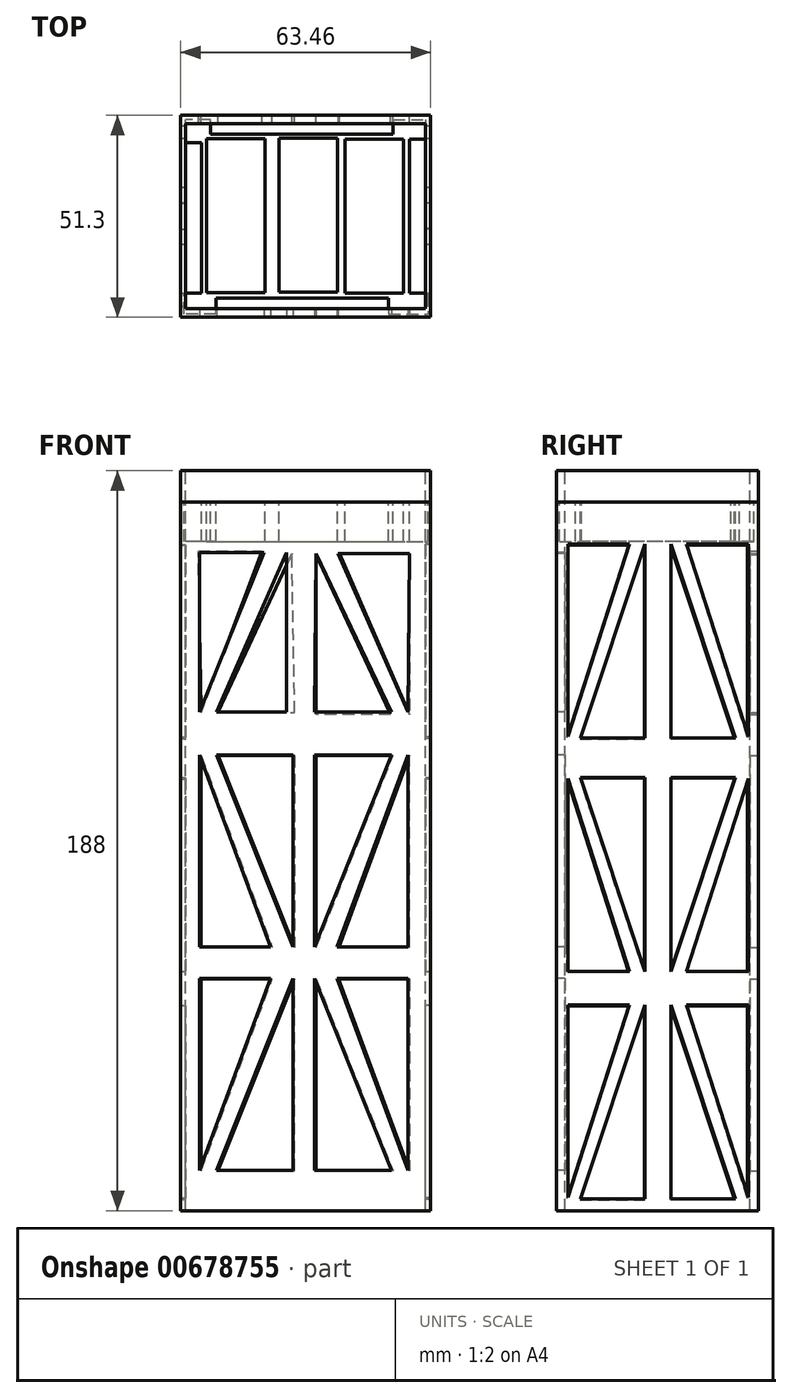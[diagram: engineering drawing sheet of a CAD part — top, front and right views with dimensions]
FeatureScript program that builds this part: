
annotation { "Feature Type Name" : "Feature", "Feature Type Description" : "" }
export const myFeature = defineFeature(function(context is Context, id is Id, definition is map)
    precondition{}
    {
        {
            var Q0;
            Q0=qCreatedBy(makeId("Top.planeOp"),FACE);
            var sketch = newSketch(context, id + "F0", { "sketchPlane" : qUnion([Q0])});
            skLineSegment(sketch, "E0.bottom", {"start": v(-30.5, 23.5) * mm, "end": v(30.5, 23.5) * mm});
            skLineSegment(sketch, "E0.top", {"start": v(-30.5, -23.5) * mm, "end": v(30.5, -23.5) * mm});
            skLineSegment(sketch, "E0.left", {"start": v(-30.5, 23.5) * mm, "end": v(-30.5, -23.5) * mm});
            skLineSegment(sketch, "E0.right", {"start": v(30.5, 23.5) * mm, "end": v(30.5, -23.5) * mm});
            skPoint(sketch, "E0.middle", {"position": v(0, 0) * mm});
            skLineSegment(sketch, "E1.bottom", {"start": v(-31.73, 25.65) * mm, "end": v(31.73, 25.65) * mm});
            skLineSegment(sketch, "E1.top", {"start": v(-31.73, -25.65) * mm, "end": v(31.73, -25.65) * mm});
            skLineSegment(sketch, "E1.left", {"start": v(-31.73, 25.65) * mm, "end": v(-31.73, -25.65) * mm});
            skLineSegment(sketch, "E1.right", {"start": v(31.73, 25.65) * mm, "end": v(31.73, -25.65) * mm});
            skSolve(sketch);
        }
        {
            var Q0;
            Q0=qSketchRegion(id+"F0",true);
            var Q1;
            Q1=qSketchRegion(id+"F2",true);
            extrude(context, id + "F1", {"entities" : qUnion([Q0, Q1]), "oppositeDirection" : true, "depth" : 180 * mm, "offsetDistance" : 25 * mm});
        }
        {
            var Q0;
            Q0=qCreatedBy(makeId("Front.planeOp"),FACE);
            var sketch = newSketch(context, id + "F2", { "sketchPlane" : qUnion([Q0])});
            skLineSegment(sketch, "E2", {"start": v(-37.52, 0) * mm, "end": v(-37.52, -20) * mm});
            skLineSegment(sketch, "E3", {"start": v(38.63, 0) * mm, "end": v(38.63, -20) * mm});
            skSolve(sketch);
        }
        {
            var Q0;
            Q0=qCreatedBy(makeId("Top.planeOp"),FACE);
            var sketch = newSketch(context, id + "F3", { "sketchPlane" : qUnion([Q0])});
            skLineSegment(sketch, "E4.bottom", {"start": v(-26.37, 20.82) * mm, "end": v(26.37, 20.82) * mm});
            skLineSegment(sketch, "E4.top", {"start": v(-26.37, -20.82) * mm, "end": v(26.37, -20.82) * mm});
            skLineSegment(sketch, "E4.left", {"start": v(-26.37, 20.82) * mm, "end": v(-26.37, -20.82) * mm});
            skLineSegment(sketch, "E4.right", {"start": v(26.37, 20.82) * mm, "end": v(26.37, -20.82) * mm});
            skPoint(sketch, "E4.middle", {"position": v(0, 0) * mm});
            skLineSegment(sketch, "E5.bottom", {"start": v(-25.17, 19.7) * mm, "end": v(-10.28, 19.7) * mm});
            skLineSegment(sketch, "E5.top", {"start": v(-25.17, -19.42) * mm, "end": v(-10.28, -19.42) * mm});
            skLineSegment(sketch, "E5.left", {"start": v(-25.17, 19.7) * mm, "end": v(-25.17, -19.42) * mm});
            skLineSegment(sketch, "E5.right", {"start": v(-10.28, 19.7) * mm, "end": v(-10.28, -19.42) * mm});
            skLineSegment(sketch, "E6.bottom", {"start": v(-6.78, 19.79) * mm, "end": v(8.12, 19.79) * mm});
            skLineSegment(sketch, "E6.top", {"start": v(-6.78, -19.34) * mm, "end": v(8.12, -19.34) * mm});
            skLineSegment(sketch, "E6.left", {"start": v(-6.78, 19.79) * mm, "end": v(-6.78, -19.34) * mm});
            skLineSegment(sketch, "E6.right", {"start": v(8.12, 19.79) * mm, "end": v(8.12, -19.34) * mm});
            skLineSegment(sketch, "E7.bottom", {"start": v(10.02, 19.6) * mm, "end": v(24.92, 19.6) * mm});
            skLineSegment(sketch, "E7.top", {"start": v(10.02, -19.52) * mm, "end": v(24.92, -19.52) * mm});
            skLineSegment(sketch, "E7.left", {"start": v(10.02, 19.6) * mm, "end": v(10.02, -19.52) * mm});
            skLineSegment(sketch, "E7.right", {"start": v(24.92, 19.6) * mm, "end": v(24.92, -19.52) * mm});
            skLineSegment(sketch, "E8.bottom", {"start": v(-26.37, 18.7) * mm, "end": v(-30.55, 18.7) * mm});
            skLineSegment(sketch, "E8.top", {"start": v(-26.37, 24.55) * mm, "end": v(-30.55, 24.55) * mm});
            skLineSegment(sketch, "E8.left", {"start": v(-26.37, 18.7) * mm, "end": v(-26.37, 24.55) * mm});
            skLineSegment(sketch, "E8.right", {"start": v(-30.55, 18.7) * mm, "end": v(-30.55, 24.55) * mm});
            skLineSegment(sketch, "E9.bottom", {"start": v(-24.14, 20.82) * mm, "end": v(-26.37, 20.82) * mm});
            skLineSegment(sketch, "E9.top", {"start": v(-24.14, 24.55) * mm, "end": v(-26.37, 24.55) * mm});
            skLineSegment(sketch, "E9.left", {"start": v(-24.14, 20.82) * mm, "end": v(-24.14, 24.55) * mm});
            skLineSegment(sketch, "E9.right", {"start": v(-26.37, 20.82) * mm, "end": v(-26.37, 24.55) * mm});
            skLineSegment(sketch, "E10.bottom", {"start": v(22.27, 24.49) * mm, "end": v(30.52, 24.49) * mm});
            skLineSegment(sketch, "E10.top", {"start": v(22.27, 19.6) * mm, "end": v(30.52, 19.6) * mm});
            skLineSegment(sketch, "E10.left", {"start": v(22.27, 24.49) * mm, "end": v(22.27, 19.6) * mm});
            skLineSegment(sketch, "E10.right", {"start": v(30.52, 24.49) * mm, "end": v(30.52, 19.6) * mm});
            skLineSegment(sketch, "E11.bottom", {"start": v(21.07, -19.52) * mm, "end": v(31.12, -19.52) * mm});
            skLineSegment(sketch, "E11.top", {"start": v(21.07, -24.85) * mm, "end": v(31.12, -24.85) * mm});
            skLineSegment(sketch, "E11.left", {"start": v(21.07, -19.52) * mm, "end": v(21.07, -24.85) * mm});
            skLineSegment(sketch, "E11.right", {"start": v(31.12, -19.52) * mm, "end": v(31.12, -24.85) * mm});
            skLineSegment(sketch, "E12.bottom", {"start": v(-22.78, -24.85) * mm, "end": v(-30.89, -24.85) * mm});
            skLineSegment(sketch, "E12.top", {"start": v(-22.78, -19.52) * mm, "end": v(-30.89, -19.52) * mm});
            skLineSegment(sketch, "E12.left", {"start": v(-22.78, -24.85) * mm, "end": v(-22.78, -19.52) * mm});
            skLineSegment(sketch, "E12.right", {"start": v(-30.89, -24.85) * mm, "end": v(-30.89, -19.52) * mm});
            skSolve(sketch);
        }
        {
            var Q0;
            Q0=qSketchRegion(id+"F3",true);
            extrude(context, id + "F4", {"entities" : qUnion([Q0]), "oppositeDirection" : true, "depth" : 10 * mm, "offsetDistance" : 25 * mm});
        }
        {
            var Q0;
            Q0=makeQuery(id+"F1.opExtrude","SWEPT_FACE",FACE,{"disambiguationData":[OSD([sQuery(id+"F0.wireOp",EDGE,"E1.top")])]});
            var sketch = newSketch(context, id + "F5", { "sketchPlane" : qUnion([Q0])});
            skLineSegment(sketch, "E13", {"start": v(-26.9, -12.74) * mm, "end": v(-10.52, -12.74) * mm});
            skLineSegment(sketch, "E14", {"start": v(-26.9, -12.74) * mm, "end": v(-26.9, -53.34) * mm});
            skLineSegment(sketch, "E15", {"start": v(-26.9, -53.34) * mm, "end": v(-10.52, -12.74) * mm});
            skLineSegment(sketch, "E16", {"start": v(-22.62, -53.34) * mm, "end": v(-4.82, -53.34) * mm});
            skLineSegment(sketch, "E17", {"start": v(-4.82, -53.34) * mm, "end": v(-4.82, -12.74) * mm});
            skLineSegment(sketch, "E18", {"start": v(-4.82, -12.74) * mm, "end": v(-22.62, -53.34) * mm});
            skLineSegment(sketch, "E19.MirrorCS", {"start": v(26.08, -53.34) * mm, "end": v(8.3, -13.02) * mm});
            skLineSegment(sketch, "E20.MirrorCS", {"start": v(21.8, -53.34) * mm, "end": v(2.32, -53.34) * mm});
            skLineSegment(sketch, "E21.MirrorCS", {"start": v(2.32, -53.34) * mm, "end": v(2.6, -13.02) * mm});
            skLineSegment(sketch, "E22.MirrorCS", {"start": v(2.6, -13.02) * mm, "end": v(21.8, -53.34) * mm});
            skLineSegment(sketch, "E23.MirrorCS", {"start": v(26.36, -13.02) * mm, "end": v(26.08, -53.34) * mm});
            skLineSegment(sketch, "E24.MirrorCS", {"start": v(26.36, -13.02) * mm, "end": v(8.3, -13.02) * mm});
            skLineSegment(sketch, "E25.MirrorCS", {"start": v(21.8, -64.27) * mm, "end": v(2.32, -64.27) * mm});
            skLineSegment(sketch, "E26.MirrorCS", {"start": v(-3.14, -112.97) * mm, "end": v(-22.62, -64.27) * mm});
            skLineSegment(sketch, "E27.MirrorCS", {"start": v(2.32, -64.27) * mm, "end": v(2.32, -112.97) * mm});
            skLineSegment(sketch, "E28.MirrorCS", {"start": v(2.32, -112.97) * mm, "end": v(21.8, -64.27) * mm});
            skLineSegment(sketch, "E29.MirrorCS", {"start": v(-3.14, -64.27) * mm, "end": v(-3.14, -112.97) * mm});
            skLineSegment(sketch, "E30.MirrorCS", {"start": v(26.08, -64.27) * mm, "end": v(8.02, -112.97) * mm});
            skLineSegment(sketch, "E31.MirrorCS", {"start": v(-26.9, -64.27) * mm, "end": v(-8.84, -112.97) * mm});
            skLineSegment(sketch, "E32.MirrorCS", {"start": v(-26.9, -112.97) * mm, "end": v(-26.9, -64.27) * mm});
            skLineSegment(sketch, "E33.MirrorCS", {"start": v(-26.9, -112.97) * mm, "end": v(-8.84, -112.97) * mm});
            skLineSegment(sketch, "E34.MirrorCS", {"start": v(26.08, -112.97) * mm, "end": v(8.02, -112.97) * mm});
            skLineSegment(sketch, "E35.MirrorCS", {"start": v(-22.62, -64.27) * mm, "end": v(-3.14, -64.27) * mm});
            skLineSegment(sketch, "E36.MirrorCS", {"start": v(26.08, -112.97) * mm, "end": v(26.08, -64.27) * mm});
            skLineSegment(sketch, "E37.MirrorCS", {"start": v(26.08, -121.05) * mm, "end": v(26.08, -169.75) * mm});
            skLineSegment(sketch, "E38.MirrorCS", {"start": v(26.08, -169.75) * mm, "end": v(8.02, -121.05) * mm});
            skLineSegment(sketch, "E39.MirrorCS", {"start": v(26.08, -121.05) * mm, "end": v(8.02, -121.05) * mm});
            skLineSegment(sketch, "E40.MirrorCS", {"start": v(2.32, -121.05) * mm, "end": v(21.8, -169.75) * mm});
            skLineSegment(sketch, "E41.MirrorCS", {"start": v(-3.14, -121.05) * mm, "end": v(-22.62, -169.75) * mm});
            skLineSegment(sketch, "E42.MirrorCS", {"start": v(-26.9, -121.05) * mm, "end": v(-26.9, -169.75) * mm});
            skLineSegment(sketch, "E43.MirrorCS", {"start": v(-3.14, -169.75) * mm, "end": v(-3.14, -121.05) * mm});
            skLineSegment(sketch, "E44.MirrorCS", {"start": v(-26.9, -169.75) * mm, "end": v(-8.84, -121.05) * mm});
            skLineSegment(sketch, "E45.MirrorCS", {"start": v(-22.62, -169.75) * mm, "end": v(-3.14, -169.75) * mm});
            skLineSegment(sketch, "E46.MirrorCS", {"start": v(-26.9, -121.05) * mm, "end": v(-8.84, -121.05) * mm});
            skLineSegment(sketch, "E47.MirrorCS", {"start": v(21.8, -169.75) * mm, "end": v(2.32, -169.75) * mm});
            skLineSegment(sketch, "E48.MirrorCS", {"start": v(2.32, -169.75) * mm, "end": v(2.32, -121.05) * mm});
            skSolve(sketch);
        }
        {
            var Q0;
            Q0=makeQuery(id+"F5.imprint","IMPRINT",FACE,{"disambiguationData":[TD([[makeQuery(id+"F5.imprint","IMPRINT",EDGE,{"derivedFrom":sQuery(id+"F5.wireOp",EDGE,"E16")}),1.0]])]});
            var Q1;
            Q1=makeQuery(id+"F5.imprint","IMPRINT",FACE,{"disambiguationData":[TD([[makeQuery(id+"F5.imprint","IMPRINT",EDGE,{"derivedFrom":sQuery(id+"F5.wireOp",EDGE,"E13")}),-1.0]])]});
            var Q2;
            Q2=makeQuery(id+"F5.imprint","IMPRINT",FACE,{"disambiguationData":[TD([[makeQuery(id+"F5.imprint","IMPRINT",EDGE,{"derivedFrom":sQuery(id+"F5.wireOp",EDGE,"E20.MirrorCS")}),-1.0]])]});
            var Q3;
            Q3=makeQuery(id+"F5.imprint","IMPRINT",FACE,{"disambiguationData":[TD([[makeQuery(id+"F5.imprint","IMPRINT",EDGE,{"derivedFrom":sQuery(id+"F5.wireOp",EDGE,"E19.MirrorCS")}),-1.0]])]});
            var Q4;
            Q4=makeQuery(id+"F5.imprint","IMPRINT",FACE,{"disambiguationData":[TD([[makeQuery(id+"F5.imprint","IMPRINT",EDGE,{"derivedFrom":sQuery(id+"F5.wireOp",EDGE,"E31.MirrorCS")}),-1.0]])]});
            var Q5;
            Q5=makeQuery(id+"F5.imprint","IMPRINT",FACE,{"disambiguationData":[TD([[makeQuery(id+"F5.imprint","IMPRINT",EDGE,{"derivedFrom":sQuery(id+"F5.wireOp",EDGE,"E26.MirrorCS")}),-1.0]])]});
            var Q6;
            Q6=makeQuery(id+"F5.imprint","IMPRINT",FACE,{"disambiguationData":[TD([[makeQuery(id+"F5.imprint","IMPRINT",EDGE,{"derivedFrom":sQuery(id+"F5.wireOp",EDGE,"E25.MirrorCS")}),1.0]])]});
            var Q7;
            Q7=makeQuery(id+"F5.imprint","IMPRINT",FACE,{"disambiguationData":[TD([[makeQuery(id+"F5.imprint","IMPRINT",EDGE,{"derivedFrom":sQuery(id+"F5.wireOp",EDGE,"E30.MirrorCS")}),1.0]])]});
            var Q8;
            Q8=makeQuery(id+"F5.imprint","IMPRINT",FACE,{"disambiguationData":[TD([[makeQuery(id+"F5.imprint","IMPRINT",EDGE,{"derivedFrom":sQuery(id+"F5.wireOp",EDGE,"E37.MirrorCS")}),-1.0]])]});
            var Q9;
            Q9=makeQuery(id+"F5.imprint","IMPRINT",FACE,{"disambiguationData":[TD([[makeQuery(id+"F5.imprint","IMPRINT",EDGE,{"derivedFrom":sQuery(id+"F5.wireOp",EDGE,"E40.MirrorCS")}),-1.0]])]});
            var Q10;
            Q10=makeQuery(id+"F5.imprint","IMPRINT",FACE,{"disambiguationData":[TD([[makeQuery(id+"F5.imprint","IMPRINT",EDGE,{"derivedFrom":sQuery(id+"F5.wireOp",EDGE,"E41.MirrorCS")}),1.0]])]});
            var Q11;
            Q11=makeQuery(id+"F5.imprint","IMPRINT",FACE,{"disambiguationData":[TD([[makeQuery(id+"F5.imprint","IMPRINT",EDGE,{"derivedFrom":sQuery(id+"F5.wireOp",EDGE,"E42.MirrorCS")}),1.0]])]});
            extrude(context, id + "F6", {"entities" : qUnion([Q0, Q1, Q2, Q3, Q4, Q5, Q6, Q7, Q8, Q9, Q10, Q11]), "oppositeDirection" : true, "depth" : 5 * mm, "offsetDistance" : 25 * mm});
        }
        {
            var Q0;
            Q0=makeQuery(id+"F6.opExtrude","SWEPT_BODY",BODY,{"disambiguationData":[OSD([sQuery(id+"F5.wireOp",EDGE,"E13"),sQuery(id+"F5.wireOp",EDGE,"E14"),sQuery(id+"F5.wireOp",EDGE,"E15")])]});
            var Q1;
            Q1=makeQuery(id+"F6.opExtrude","SWEPT_BODY",BODY,{"disambiguationData":[OSD([sQuery(id+"F5.wireOp",EDGE,"E16"),sQuery(id+"F5.wireOp",EDGE,"E17"),sQuery(id+"F5.wireOp",EDGE,"E18")])]});
            var Q2;
            Q2=makeQuery(id+"F6.opExtrude","SWEPT_BODY",BODY,{"disambiguationData":[OSD([sQuery(id+"F5.wireOp",EDGE,"E20.MirrorCS"),sQuery(id+"F5.wireOp",EDGE,"E21.MirrorCS"),sQuery(id+"F5.wireOp",EDGE,"E22.MirrorCS")])]});
            var Q3;
            Q3=makeQuery(id+"F6.opExtrude","SWEPT_BODY",BODY,{"disambiguationData":[OSD([sQuery(id+"F5.wireOp",EDGE,"E19.MirrorCS"),sQuery(id+"F5.wireOp",EDGE,"E23.MirrorCS"),sQuery(id+"F5.wireOp",EDGE,"E24.MirrorCS")])]});
            var Q4;
            Q4=makeQuery(id+"F6.opExtrude","SWEPT_BODY",BODY,{"disambiguationData":[OSD([sQuery(id+"F5.wireOp",EDGE,"E30.MirrorCS"),sQuery(id+"F5.wireOp",EDGE,"E34.MirrorCS"),sQuery(id+"F5.wireOp",EDGE,"E36.MirrorCS")])]});
            var Q5;
            Q5=makeQuery(id+"F6.opExtrude","SWEPT_BODY",BODY,{"disambiguationData":[OSD([sQuery(id+"F5.wireOp",EDGE,"E25.MirrorCS"),sQuery(id+"F5.wireOp",EDGE,"E27.MirrorCS"),sQuery(id+"F5.wireOp",EDGE,"E28.MirrorCS")])]});
            var Q6;
            Q6=makeQuery(id+"F6.opExtrude","SWEPT_BODY",BODY,{"disambiguationData":[OSD([sQuery(id+"F5.wireOp",EDGE,"E26.MirrorCS"),sQuery(id+"F5.wireOp",EDGE,"E29.MirrorCS"),sQuery(id+"F5.wireOp",EDGE,"E35.MirrorCS")])]});
            var Q7;
            Q7=makeQuery(id+"F6.opExtrude","SWEPT_BODY",BODY,{"disambiguationData":[OSD([sQuery(id+"F5.wireOp",EDGE,"E31.MirrorCS"),sQuery(id+"F5.wireOp",EDGE,"E32.MirrorCS"),sQuery(id+"F5.wireOp",EDGE,"E33.MirrorCS")])]});
            var Q8;
            Q8=makeQuery(id+"F6.opExtrude","SWEPT_BODY",BODY,{"disambiguationData":[OSD([sQuery(id+"F5.wireOp",EDGE,"E42.MirrorCS"),sQuery(id+"F5.wireOp",EDGE,"E44.MirrorCS"),sQuery(id+"F5.wireOp",EDGE,"E46.MirrorCS")])]});
            var Q9;
            Q9=makeQuery(id+"F6.opExtrude","SWEPT_BODY",BODY,{"disambiguationData":[OSD([sQuery(id+"F5.wireOp",EDGE,"E41.MirrorCS"),sQuery(id+"F5.wireOp",EDGE,"E43.MirrorCS"),sQuery(id+"F5.wireOp",EDGE,"E45.MirrorCS")])]});
            var Q10;
            Q10=makeQuery(id+"F6.opExtrude","SWEPT_BODY",BODY,{"disambiguationData":[OSD([sQuery(id+"F5.wireOp",EDGE,"E40.MirrorCS"),sQuery(id+"F5.wireOp",EDGE,"E47.MirrorCS"),sQuery(id+"F5.wireOp",EDGE,"E48.MirrorCS")])]});
            var Q11;
            Q11=makeQuery(id+"F6.opExtrude","SWEPT_BODY",BODY,{"disambiguationData":[OSD([sQuery(id+"F5.wireOp",EDGE,"E37.MirrorCS"),sQuery(id+"F5.wireOp",EDGE,"E38.MirrorCS"),sQuery(id+"F5.wireOp",EDGE,"E39.MirrorCS")])]});
            var Q12;
            Q12=makeQuery(id+"F1.opExtrude","SWEPT_BODY",BODY,{"disambiguationData":[OSD([sQuery(id+"F0.wireOp",EDGE,"E0.bottom"),sQuery(id+"F0.wireOp",EDGE,"E0.top"),sQuery(id+"F0.wireOp",EDGE,"E0.left"),sQuery(id+"F0.wireOp",EDGE,"E0.right"),sQuery(id+"F0.wireOp",EDGE,"E1.bottom"),sQuery(id+"F0.wireOp",EDGE,"E1.top"),sQuery(id+"F0.wireOp",EDGE,"E1.left"),sQuery(id+"F0.wireOp",EDGE,"E1.right")])]});
            booleanBodies(context, id + "F7", {"operationType" : BooleanOperationType.SUBTRACTION, "tools" : qUnion([Q0, Q1, Q2, Q3, Q4, Q5, Q6, Q7, Q8, Q9, Q10, Q11]), "targets" : qUnion([Q12])});
        }
        {
            var Q0;
            Q0=makeQuery(id+"F1.opExtrude","SWEPT_FACE",FACE,{"disambiguationData":[OSD([sQuery(id+"F0.wireOp",EDGE,"E1.left")])]});
            var sketch = newSketch(context, id + "F8", { "sketchPlane" : qUnion([Q0])});
            skLineSegment(sketch, "E49", {"start": v(-22.91, -10.86) * mm, "end": v(-22.91, -59.77) * mm});
            skLineSegment(sketch, "E50", {"start": v(-22.91, -59.77) * mm, "end": v(-7.26, -10.86) * mm});
            skLineSegment(sketch, "E51", {"start": v(-7.26, -10.86) * mm, "end": v(-22.91, -10.86) * mm});
            skLineSegment(sketch, "E52", {"start": v(-3.33, -10.86) * mm, "end": v(-19.7, -60.13) * mm});
            skLineSegment(sketch, "E53", {"start": v(-19.7, -60.13) * mm, "end": v(-3.33, -60.13) * mm});
            skLineSegment(sketch, "E54", {"start": v(-3.33, -60.13) * mm, "end": v(-3.33, -10.86) * mm});
            skLineSegment(sketch, "E55.MirrorCS", {"start": v(22.91, -59.77) * mm, "end": v(7.25, -10.83) * mm});
            skLineSegment(sketch, "E56.MirrorCS", {"start": v(7.25, -10.83) * mm, "end": v(22.91, -10.83) * mm});
            skLineSegment(sketch, "E57.MirrorCS", {"start": v(3.33, -10.83) * mm, "end": v(19.7, -60.13) * mm});
            skLineSegment(sketch, "E58.MirrorCS", {"start": v(3.33, -60.13) * mm, "end": v(3.33, -10.83) * mm});
            skLineSegment(sketch, "E59.MirrorCS", {"start": v(19.7, -60.13) * mm, "end": v(3.33, -60.13) * mm});
            skLineSegment(sketch, "E60.MirrorCS", {"start": v(22.91, -10.83) * mm, "end": v(22.91, -59.77) * mm});
            skLineSegment(sketch, "E61.MirrorCS", {"start": v(-22.91, -119.4) * mm, "end": v(-22.91, -70.45) * mm});
            skLineSegment(sketch, "E62.MirrorCS", {"start": v(-19.7, -70.1) * mm, "end": v(-3.33, -70.1) * mm});
            skLineSegment(sketch, "E63.MirrorCS", {"start": v(-22.91, -70.45) * mm, "end": v(-7.25, -119.4) * mm});
            skLineSegment(sketch, "E64.MirrorCS", {"start": v(-3.33, -119.4) * mm, "end": v(-19.7, -70.1) * mm});
            skLineSegment(sketch, "E65.MirrorCS", {"start": v(-7.25, -119.4) * mm, "end": v(-22.91, -119.4) * mm});
            skLineSegment(sketch, "E66.MirrorCS", {"start": v(-3.33, -70.1) * mm, "end": v(-3.33, -119.4) * mm});
            skLineSegment(sketch, "E67.MirrorCS", {"start": v(3.33, -119.4) * mm, "end": v(19.7, -70.1) * mm});
            skLineSegment(sketch, "E68.MirrorCS", {"start": v(22.91, -119.4) * mm, "end": v(22.91, -70.45) * mm});
            skLineSegment(sketch, "E69.MirrorCS", {"start": v(7.25, -119.4) * mm, "end": v(22.91, -119.4) * mm});
            skLineSegment(sketch, "E70.MirrorCS", {"start": v(3.33, -70.1) * mm, "end": v(3.33, -119.4) * mm});
            skLineSegment(sketch, "E71.MirrorCS", {"start": v(22.91, -70.45) * mm, "end": v(7.25, -119.4) * mm});
            skLineSegment(sketch, "E72.MirrorCS", {"start": v(19.7, -70.1) * mm, "end": v(3.33, -70.1) * mm});
            skLineSegment(sketch, "E73.MirrorCS", {"start": v(22.91, -127.94) * mm, "end": v(22.91, -176.88) * mm});
            skLineSegment(sketch, "E74.MirrorCS", {"start": v(3.33, -177.24) * mm, "end": v(3.33, -127.94) * mm});
            skLineSegment(sketch, "E75.MirrorCS", {"start": v(3.33, -127.94) * mm, "end": v(19.7, -177.24) * mm});
            skLineSegment(sketch, "E76.MirrorCS", {"start": v(-22.91, -127.94) * mm, "end": v(-22.91, -176.88) * mm});
            skLineSegment(sketch, "E77.MirrorCS", {"start": v(-7.25, -127.94) * mm, "end": v(-22.91, -127.94) * mm});
            skLineSegment(sketch, "E78.MirrorCS", {"start": v(22.91, -176.88) * mm, "end": v(7.25, -127.94) * mm});
            skLineSegment(sketch, "E79.MirrorCS", {"start": v(-19.7, -177.24) * mm, "end": v(-3.33, -177.24) * mm});
            skLineSegment(sketch, "E80.MirrorCS", {"start": v(-3.33, -177.24) * mm, "end": v(-3.33, -127.94) * mm});
            skLineSegment(sketch, "E81.MirrorCS", {"start": v(-22.91, -176.88) * mm, "end": v(-7.25, -127.94) * mm});
            skLineSegment(sketch, "E82.MirrorCS", {"start": v(19.7, -177.24) * mm, "end": v(3.33, -177.24) * mm});
            skLineSegment(sketch, "E83.MirrorCS", {"start": v(-3.33, -127.94) * mm, "end": v(-19.7, -177.24) * mm});
            skLineSegment(sketch, "E84.MirrorCS", {"start": v(7.25, -127.94) * mm, "end": v(22.91, -127.94) * mm});
            skSolve(sketch);
        }
        {
            var Q0;
            Q0=makeQuery(id+"F8.imprint","IMPRINT",FACE,{"disambiguationData":[TD([[makeQuery(id+"F8.imprint","IMPRINT",EDGE,{"derivedFrom":sQuery(id+"F8.wireOp",EDGE,"E52")}),1.0]])]});
            var Q1;
            Q1=makeQuery(id+"F8.imprint","IMPRINT",FACE,{"disambiguationData":[TD([[makeQuery(id+"F8.imprint","IMPRINT",EDGE,{"derivedFrom":sQuery(id+"F8.wireOp",EDGE,"E57.MirrorCS")}),-1.0]])]});
            var Q2;
            Q2=makeQuery(id+"F8.imprint","IMPRINT",FACE,{"disambiguationData":[TD([[makeQuery(id+"F8.imprint","IMPRINT",EDGE,{"derivedFrom":sQuery(id+"F8.wireOp",EDGE,"E55.MirrorCS")}),-1.0]])]});
            var Q3;
            Q3=makeQuery(id+"F8.imprint","IMPRINT",FACE,{"disambiguationData":[TD([[makeQuery(id+"F8.imprint","IMPRINT",EDGE,{"derivedFrom":sQuery(id+"F8.wireOp",EDGE,"E62.MirrorCS")}),-1.0]])]});
            var Q4;
            Q4=makeQuery(id+"F8.imprint","IMPRINT",FACE,{"disambiguationData":[TD([[makeQuery(id+"F8.imprint","IMPRINT",EDGE,{"derivedFrom":sQuery(id+"F8.wireOp",EDGE,"E61.MirrorCS")}),-1.0]])]});
            var Q5;
            Q5=makeQuery(id+"F8.imprint","IMPRINT",FACE,{"disambiguationData":[TD([[makeQuery(id+"F8.imprint","IMPRINT",EDGE,{"derivedFrom":sQuery(id+"F8.wireOp",EDGE,"E68.MirrorCS")}),1.0]])]});
            var Q6;
            Q6=makeQuery(id+"F8.imprint","IMPRINT",FACE,{"disambiguationData":[TD([[makeQuery(id+"F8.imprint","IMPRINT",EDGE,{"derivedFrom":sQuery(id+"F8.wireOp",EDGE,"E76.MirrorCS")}),1.0]])]});
            var Q7;
            Q7=makeQuery(id+"F8.imprint","IMPRINT",FACE,{"disambiguationData":[TD([[makeQuery(id+"F8.imprint","IMPRINT",EDGE,{"derivedFrom":sQuery(id+"F8.wireOp",EDGE,"E79.MirrorCS")}),1.0]])]});
            var Q8;
            Q8=makeQuery(id+"F8.imprint","IMPRINT",FACE,{"disambiguationData":[TD([[makeQuery(id+"F8.imprint","IMPRINT",EDGE,{"derivedFrom":sQuery(id+"F8.wireOp",EDGE,"E74.MirrorCS")}),-1.0]])]});
            var Q9;
            Q9=makeQuery(id+"F8.imprint","IMPRINT",FACE,{"disambiguationData":[TD([[makeQuery(id+"F8.imprint","IMPRINT",EDGE,{"derivedFrom":sQuery(id+"F8.wireOp",EDGE,"E73.MirrorCS")}),-1.0]])]});
            var Q10;
            Q10=makeQuery(id+"F8.imprint","IMPRINT",FACE,{"disambiguationData":[TD([[makeQuery(id+"F8.imprint","IMPRINT",EDGE,{"derivedFrom":sQuery(id+"F8.wireOp",EDGE,"E67.MirrorCS")}),1.0]])]});
            var Q11;
            Q11=makeQuery(id+"F8.imprint","IMPRINT",FACE,{"disambiguationData":[TD([[makeQuery(id+"F8.imprint","IMPRINT",EDGE,{"derivedFrom":sQuery(id+"F8.wireOp",EDGE,"E49")}),1.0]])]});
            extrude(context, id + "F9", {"entities" : qUnion([Q0, Q1, Q2, Q3, Q4, Q5, Q6, Q7, Q8, Q9, Q10, Q11]), "oppositeDirection" : true, "depth" : 5 * mm, "offsetDistance" : 25 * mm});
        }
        {
            var Q0;
            Q0=makeQuery(id+"F9.opExtrude","SWEPT_BODY",BODY,{"disambiguationData":[OSD([sQuery(id+"F8.wireOp",EDGE,"E52"),sQuery(id+"F8.wireOp",EDGE,"E53"),sQuery(id+"F8.wireOp",EDGE,"E54")])]});
            var Q1;
            Q1=makeQuery(id+"F9.opExtrude","SWEPT_BODY",BODY,{"disambiguationData":[OSD([sQuery(id+"F8.wireOp",EDGE,"E57.MirrorCS"),sQuery(id+"F8.wireOp",EDGE,"E58.MirrorCS"),sQuery(id+"F8.wireOp",EDGE,"E59.MirrorCS")])]});
            var Q2;
            Q2=makeQuery(id+"F9.opExtrude","SWEPT_BODY",BODY,{"disambiguationData":[OSD([sQuery(id+"F8.wireOp",EDGE,"E55.MirrorCS"),sQuery(id+"F8.wireOp",EDGE,"E56.MirrorCS"),sQuery(id+"F8.wireOp",EDGE,"E60.MirrorCS")])]});
            var Q3;
            Q3=makeQuery(id+"F9.opExtrude","SWEPT_BODY",BODY,{"disambiguationData":[OSD([sQuery(id+"F8.wireOp",EDGE,"E49"),sQuery(id+"F8.wireOp",EDGE,"E50"),sQuery(id+"F8.wireOp",EDGE,"E51")])]});
            var Q4;
            Q4=makeQuery(id+"F9.opExtrude","SWEPT_BODY",BODY,{"disambiguationData":[OSD([sQuery(id+"F8.wireOp",EDGE,"E61.MirrorCS"),sQuery(id+"F8.wireOp",EDGE,"E63.MirrorCS"),sQuery(id+"F8.wireOp",EDGE,"E65.MirrorCS")])]});
            var Q5;
            Q5=makeQuery(id+"F9.opExtrude","SWEPT_BODY",BODY,{"disambiguationData":[OSD([sQuery(id+"F8.wireOp",EDGE,"E62.MirrorCS"),sQuery(id+"F8.wireOp",EDGE,"E64.MirrorCS"),sQuery(id+"F8.wireOp",EDGE,"E66.MirrorCS")])]});
            var Q6;
            Q6=makeQuery(id+"F9.opExtrude","SWEPT_BODY",BODY,{"disambiguationData":[OSD([sQuery(id+"F8.wireOp",EDGE,"E67.MirrorCS"),sQuery(id+"F8.wireOp",EDGE,"E70.MirrorCS"),sQuery(id+"F8.wireOp",EDGE,"E72.MirrorCS")])]});
            var Q7;
            Q7=makeQuery(id+"F9.opExtrude","SWEPT_BODY",BODY,{"disambiguationData":[OSD([sQuery(id+"F8.wireOp",EDGE,"E68.MirrorCS"),sQuery(id+"F8.wireOp",EDGE,"E69.MirrorCS"),sQuery(id+"F8.wireOp",EDGE,"E71.MirrorCS")])]});
            var Q8;
            Q8=makeQuery(id+"F9.opExtrude","SWEPT_BODY",BODY,{"disambiguationData":[OSD([sQuery(id+"F8.wireOp",EDGE,"E73.MirrorCS"),sQuery(id+"F8.wireOp",EDGE,"E78.MirrorCS"),sQuery(id+"F8.wireOp",EDGE,"E84.MirrorCS")])]});
            var Q9;
            Q9=makeQuery(id+"F9.opExtrude","SWEPT_BODY",BODY,{"disambiguationData":[OSD([sQuery(id+"F8.wireOp",EDGE,"E74.MirrorCS"),sQuery(id+"F8.wireOp",EDGE,"E75.MirrorCS"),sQuery(id+"F8.wireOp",EDGE,"E82.MirrorCS")])]});
            var Q10;
            Q10=makeQuery(id+"F9.opExtrude","SWEPT_BODY",BODY,{"disambiguationData":[OSD([sQuery(id+"F8.wireOp",EDGE,"E79.MirrorCS"),sQuery(id+"F8.wireOp",EDGE,"E80.MirrorCS"),sQuery(id+"F8.wireOp",EDGE,"E83.MirrorCS")])]});
            var Q11;
            Q11=makeQuery(id+"F9.opExtrude","SWEPT_BODY",BODY,{"disambiguationData":[OSD([sQuery(id+"F8.wireOp",EDGE,"E76.MirrorCS"),sQuery(id+"F8.wireOp",EDGE,"E77.MirrorCS"),sQuery(id+"F8.wireOp",EDGE,"E81.MirrorCS")])]});
            var Q12;
            Q12=makeQuery(id+"F1.opExtrude","SWEPT_BODY",BODY,{"disambiguationData":[OSD([sQuery(id+"F0.wireOp",EDGE,"E0.bottom"),sQuery(id+"F0.wireOp",EDGE,"E0.top"),sQuery(id+"F0.wireOp",EDGE,"E0.left"),sQuery(id+"F0.wireOp",EDGE,"E0.right"),sQuery(id+"F0.wireOp",EDGE,"E1.bottom"),sQuery(id+"F0.wireOp",EDGE,"E1.top"),sQuery(id+"F0.wireOp",EDGE,"E1.left"),sQuery(id+"F0.wireOp",EDGE,"E1.right")])]});
            booleanBodies(context, id + "F10", {"operationType" : BooleanOperationType.SUBTRACTION, "tools" : qUnion([Q0, Q1, Q2, Q3, Q4, Q5, Q6, Q7, Q8, Q9, Q10, Q11]), "targets" : qUnion([Q12])});
        }
        {
            var Q0;
            Q0=makeQuery(id+"F1.opExtrude","SWEPT_FACE",FACE,{"disambiguationData":[OSD([sQuery(id+"F0.wireOp",EDGE,"E1.right")])]});
            var sketch = newSketch(context, id + "F11", { "sketchPlane" : qUnion([Q0])});
            skLineSegment(sketch, "E85", {"start": v(-22.75, -10.65) * mm, "end": v(-22.75, -59.56) * mm});
            skLineSegment(sketch, "E86", {"start": v(-22.75, -59.56) * mm, "end": v(-7.1, -10.65) * mm});
            skLineSegment(sketch, "E87", {"start": v(-7.1, -10.65) * mm, "end": v(-22.75, -10.65) * mm});
            skLineSegment(sketch, "E88", {"start": v(-3.17, -10.65) * mm, "end": v(-19.54, -59.92) * mm});
            skLineSegment(sketch, "E89", {"start": v(-19.54, -59.92) * mm, "end": v(-3.17, -59.92) * mm});
            skLineSegment(sketch, "E90", {"start": v(-3.17, -59.92) * mm, "end": v(-3.17, -10.65) * mm});
            skLineSegment(sketch, "E91.MirrorCS", {"start": v(23.08, -59.56) * mm, "end": v(7.42, -10.62) * mm});
            skLineSegment(sketch, "E92.MirrorCS", {"start": v(7.42, -10.62) * mm, "end": v(23.08, -10.62) * mm});
            skLineSegment(sketch, "E93.MirrorCS", {"start": v(3.5, -10.62) * mm, "end": v(19.87, -59.92) * mm});
            skLineSegment(sketch, "E94.MirrorCS", {"start": v(3.5, -59.92) * mm, "end": v(3.5, -10.62) * mm});
            skLineSegment(sketch, "E95.MirrorCS", {"start": v(19.87, -59.92) * mm, "end": v(3.5, -59.92) * mm});
            skLineSegment(sketch, "E96.MirrorCS", {"start": v(23.08, -10.62) * mm, "end": v(23.08, -59.56) * mm});
            skLineSegment(sketch, "E97.MirrorCS", {"start": v(-22.75, -119.19) * mm, "end": v(-22.75, -70.24) * mm});
            skLineSegment(sketch, "E98.MirrorCS", {"start": v(-19.54, -69.88) * mm, "end": v(-3.17, -69.88) * mm});
            skLineSegment(sketch, "E99.MirrorCS", {"start": v(-22.75, -70.24) * mm, "end": v(-7.09, -119.19) * mm});
            skLineSegment(sketch, "E100.MirrorCS", {"start": v(-3.17, -119.19) * mm, "end": v(-19.54, -69.88) * mm});
            skLineSegment(sketch, "E101.MirrorCS", {"start": v(-7.09, -119.19) * mm, "end": v(-22.75, -119.19) * mm});
            skLineSegment(sketch, "E102.MirrorCS", {"start": v(-3.17, -69.88) * mm, "end": v(-3.17, -119.19) * mm});
            skLineSegment(sketch, "E103.MirrorCS", {"start": v(3.5, -119.19) * mm, "end": v(19.87, -69.88) * mm});
            skLineSegment(sketch, "E104.MirrorCS", {"start": v(23.08, -119.19) * mm, "end": v(23.08, -70.24) * mm});
            skLineSegment(sketch, "E105.MirrorCS", {"start": v(7.42, -119.19) * mm, "end": v(23.08, -119.19) * mm});
            skLineSegment(sketch, "E106.MirrorCS", {"start": v(3.5, -69.88) * mm, "end": v(3.5, -119.19) * mm});
            skLineSegment(sketch, "E107.MirrorCS", {"start": v(23.08, -70.24) * mm, "end": v(7.42, -119.19) * mm});
            skLineSegment(sketch, "E108.MirrorCS", {"start": v(19.87, -69.88) * mm, "end": v(3.5, -69.88) * mm});
            skLineSegment(sketch, "E109.MirrorCS", {"start": v(23.08, -127.73) * mm, "end": v(23.08, -176.67) * mm});
            skLineSegment(sketch, "E110.MirrorCS", {"start": v(3.5, -177.03) * mm, "end": v(3.5, -127.73) * mm});
            skLineSegment(sketch, "E111.MirrorCS", {"start": v(3.5, -127.73) * mm, "end": v(19.87, -177.03) * mm});
            skLineSegment(sketch, "E112.MirrorCS", {"start": v(-22.75, -127.73) * mm, "end": v(-22.75, -176.67) * mm});
            skLineSegment(sketch, "E113.MirrorCS", {"start": v(-7.09, -127.73) * mm, "end": v(-22.75, -127.73) * mm});
            skLineSegment(sketch, "E114.MirrorCS", {"start": v(23.08, -176.67) * mm, "end": v(7.42, -127.73) * mm});
            skLineSegment(sketch, "E115.MirrorCS", {"start": v(-19.54, -177.03) * mm, "end": v(-3.17, -177.03) * mm});
            skLineSegment(sketch, "E116.MirrorCS", {"start": v(-3.17, -177.03) * mm, "end": v(-3.17, -127.73) * mm});
            skLineSegment(sketch, "E117.MirrorCS", {"start": v(-22.75, -176.67) * mm, "end": v(-7.09, -127.73) * mm});
            skLineSegment(sketch, "E118.MirrorCS", {"start": v(19.87, -177.03) * mm, "end": v(3.5, -177.03) * mm});
            skLineSegment(sketch, "E119.MirrorCS", {"start": v(-3.17, -127.73) * mm, "end": v(-19.54, -177.03) * mm});
            skLineSegment(sketch, "E120.MirrorCS", {"start": v(7.42, -127.73) * mm, "end": v(23.08, -127.73) * mm});
            skSolve(sketch);
        }
        {
            var Q0;
            Q0=makeQuery(id+"F11.imprint","IMPRINT",FACE,{"disambiguationData":[TD([[makeQuery(id+"F11.imprint","IMPRINT",EDGE,{"derivedFrom":sQuery(id+"F11.wireOp",EDGE,"E85")}),1.0]])]});
            var Q1;
            Q1=makeQuery(id+"F11.imprint","IMPRINT",FACE,{"disambiguationData":[TD([[makeQuery(id+"F11.imprint","IMPRINT",EDGE,{"derivedFrom":sQuery(id+"F11.wireOp",EDGE,"E88")}),1.0]])]});
            var Q2;
            Q2=makeQuery(id+"F11.imprint","IMPRINT",FACE,{"disambiguationData":[TD([[makeQuery(id+"F11.imprint","IMPRINT",EDGE,{"derivedFrom":sQuery(id+"F11.wireOp",EDGE,"E93.MirrorCS")}),-1.0]])]});
            var Q3;
            Q3=makeQuery(id+"F11.imprint","IMPRINT",FACE,{"disambiguationData":[TD([[makeQuery(id+"F11.imprint","IMPRINT",EDGE,{"derivedFrom":sQuery(id+"F11.wireOp",EDGE,"E91.MirrorCS")}),-1.0]])]});
            var Q4;
            Q4=makeQuery(id+"F11.imprint","IMPRINT",FACE,{"disambiguationData":[TD([[makeQuery(id+"F11.imprint","IMPRINT",EDGE,{"derivedFrom":sQuery(id+"F11.wireOp",EDGE,"E97.MirrorCS")}),-1.0]])]});
            var Q5;
            Q5=makeQuery(id+"F11.imprint","IMPRINT",FACE,{"disambiguationData":[TD([[makeQuery(id+"F11.imprint","IMPRINT",EDGE,{"derivedFrom":sQuery(id+"F11.wireOp",EDGE,"E98.MirrorCS")}),-1.0]])]});
            var Q6;
            Q6=makeQuery(id+"F11.imprint","IMPRINT",FACE,{"disambiguationData":[TD([[makeQuery(id+"F11.imprint","IMPRINT",EDGE,{"derivedFrom":sQuery(id+"F11.wireOp",EDGE,"E103.MirrorCS")}),1.0]])]});
            var Q7;
            Q7=makeQuery(id+"F11.imprint","IMPRINT",FACE,{"disambiguationData":[TD([[makeQuery(id+"F11.imprint","IMPRINT",EDGE,{"derivedFrom":sQuery(id+"F11.wireOp",EDGE,"E104.MirrorCS")}),1.0]])]});
            var Q8;
            Q8=makeQuery(id+"F11.imprint","IMPRINT",FACE,{"disambiguationData":[TD([[makeQuery(id+"F11.imprint","IMPRINT",EDGE,{"derivedFrom":sQuery(id+"F11.wireOp",EDGE,"E109.MirrorCS")}),-1.0]])]});
            var Q9;
            Q9=makeQuery(id+"F11.imprint","IMPRINT",FACE,{"disambiguationData":[TD([[makeQuery(id+"F11.imprint","IMPRINT",EDGE,{"derivedFrom":sQuery(id+"F11.wireOp",EDGE,"E110.MirrorCS")}),-1.0]])]});
            var Q10;
            Q10=makeQuery(id+"F11.imprint","IMPRINT",FACE,{"disambiguationData":[TD([[makeQuery(id+"F11.imprint","IMPRINT",EDGE,{"derivedFrom":sQuery(id+"F11.wireOp",EDGE,"E115.MirrorCS")}),1.0]])]});
            var Q11;
            Q11=makeQuery(id+"F11.imprint","IMPRINT",FACE,{"disambiguationData":[TD([[makeQuery(id+"F11.imprint","IMPRINT",EDGE,{"derivedFrom":sQuery(id+"F11.wireOp",EDGE,"E112.MirrorCS")}),1.0]])]});
            extrude(context, id + "F12", {"entities" : qUnion([Q0, Q1, Q2, Q3, Q4, Q5, Q6, Q7, Q8, Q9, Q10, Q11]), "oppositeDirection" : true, "depth" : 5 * mm, "offsetDistance" : 25 * mm});
        }
        {
            var Q0;
            Q0=makeQuery(id+"F12.opExtrude","SWEPT_BODY",BODY,{"disambiguationData":[OSD([sQuery(id+"F11.wireOp",EDGE,"E85"),sQuery(id+"F11.wireOp",EDGE,"E86"),sQuery(id+"F11.wireOp",EDGE,"E87")])]});
            var Q1;
            Q1=makeQuery(id+"F12.opExtrude","SWEPT_BODY",BODY,{"disambiguationData":[OSD([sQuery(id+"F11.wireOp",EDGE,"E88"),sQuery(id+"F11.wireOp",EDGE,"E89"),sQuery(id+"F11.wireOp",EDGE,"E90")])]});
            var Q2;
            Q2=makeQuery(id+"F12.opExtrude","SWEPT_BODY",BODY,{"disambiguationData":[OSD([sQuery(id+"F11.wireOp",EDGE,"E93.MirrorCS"),sQuery(id+"F11.wireOp",EDGE,"E94.MirrorCS"),sQuery(id+"F11.wireOp",EDGE,"E95.MirrorCS")])]});
            var Q3;
            Q3=makeQuery(id+"F12.opExtrude","SWEPT_BODY",BODY,{"disambiguationData":[OSD([sQuery(id+"F11.wireOp",EDGE,"E91.MirrorCS"),sQuery(id+"F11.wireOp",EDGE,"E92.MirrorCS"),sQuery(id+"F11.wireOp",EDGE,"E96.MirrorCS")])]});
            var Q4;
            Q4=makeQuery(id+"F12.opExtrude","SWEPT_BODY",BODY,{"disambiguationData":[OSD([sQuery(id+"F11.wireOp",EDGE,"E97.MirrorCS"),sQuery(id+"F11.wireOp",EDGE,"E99.MirrorCS"),sQuery(id+"F11.wireOp",EDGE,"E101.MirrorCS")])]});
            var Q5;
            Q5=makeQuery(id+"F12.opExtrude","SWEPT_BODY",BODY,{"disambiguationData":[OSD([sQuery(id+"F11.wireOp",EDGE,"E98.MirrorCS"),sQuery(id+"F11.wireOp",EDGE,"E100.MirrorCS"),sQuery(id+"F11.wireOp",EDGE,"E102.MirrorCS")])]});
            var Q6;
            Q6=makeQuery(id+"F12.opExtrude","SWEPT_BODY",BODY,{"disambiguationData":[OSD([sQuery(id+"F11.wireOp",EDGE,"E103.MirrorCS"),sQuery(id+"F11.wireOp",EDGE,"E106.MirrorCS"),sQuery(id+"F11.wireOp",EDGE,"E108.MirrorCS")])]});
            var Q7;
            Q7=makeQuery(id+"F12.opExtrude","SWEPT_BODY",BODY,{"disambiguationData":[OSD([sQuery(id+"F11.wireOp",EDGE,"E104.MirrorCS"),sQuery(id+"F11.wireOp",EDGE,"E105.MirrorCS"),sQuery(id+"F11.wireOp",EDGE,"E107.MirrorCS")])]});
            var Q8;
            Q8=makeQuery(id+"F12.opExtrude","SWEPT_BODY",BODY,{"disambiguationData":[OSD([sQuery(id+"F11.wireOp",EDGE,"E109.MirrorCS"),sQuery(id+"F11.wireOp",EDGE,"E114.MirrorCS"),sQuery(id+"F11.wireOp",EDGE,"E120.MirrorCS")])]});
            var Q9;
            Q9=makeQuery(id+"F12.opExtrude","SWEPT_BODY",BODY,{"disambiguationData":[OSD([sQuery(id+"F11.wireOp",EDGE,"E110.MirrorCS"),sQuery(id+"F11.wireOp",EDGE,"E111.MirrorCS"),sQuery(id+"F11.wireOp",EDGE,"E118.MirrorCS")])]});
            var Q10;
            Q10=makeQuery(id+"F12.opExtrude","SWEPT_BODY",BODY,{"disambiguationData":[OSD([sQuery(id+"F11.wireOp",EDGE,"E115.MirrorCS"),sQuery(id+"F11.wireOp",EDGE,"E116.MirrorCS"),sQuery(id+"F11.wireOp",EDGE,"E119.MirrorCS")])]});
            var Q11;
            Q11=makeQuery(id+"F12.opExtrude","SWEPT_BODY",BODY,{"disambiguationData":[OSD([sQuery(id+"F11.wireOp",EDGE,"E112.MirrorCS"),sQuery(id+"F11.wireOp",EDGE,"E113.MirrorCS"),sQuery(id+"F11.wireOp",EDGE,"E117.MirrorCS")])]});
            var Q12;
            Q12=makeQuery(id+"F1.opExtrude","SWEPT_BODY",BODY,{"disambiguationData":[OSD([sQuery(id+"F0.wireOp",EDGE,"E0.bottom"),sQuery(id+"F0.wireOp",EDGE,"E0.top"),sQuery(id+"F0.wireOp",EDGE,"E0.left"),sQuery(id+"F0.wireOp",EDGE,"E0.right"),sQuery(id+"F0.wireOp",EDGE,"E1.bottom"),sQuery(id+"F0.wireOp",EDGE,"E1.top"),sQuery(id+"F0.wireOp",EDGE,"E1.left"),sQuery(id+"F0.wireOp",EDGE,"E1.right")])]});
            booleanBodies(context, id + "F13", {"operationType" : BooleanOperationType.SUBTRACTION, "tools" : qUnion([Q0, Q1, Q2, Q3, Q4, Q5, Q6, Q7, Q8, Q9, Q10, Q11]), "targets" : qUnion([Q12])});
        }
        {
            var Q0;
            Q0=makeQuery(id+"F1.opExtrude","SWEPT_FACE",FACE,{"disambiguationData":[OSD([sQuery(id+"F0.wireOp",EDGE,"E1.bottom")])]});
            var sketch = newSketch(context, id + "F14", { "sketchPlane" : qUnion([Q0])});
            skLineSegment(sketch, "E121", {"start": v(-26.45, -13.07) * mm, "end": v(-8.63, -13.07) * mm});
            skLineSegment(sketch, "E122", {"start": v(-26.45, -13.07) * mm, "end": v(-26.45, -53.88) * mm});
            skLineSegment(sketch, "E123", {"start": v(-26.45, -53.88) * mm, "end": v(-8.63, -13.07) * mm});
            skLineSegment(sketch, "E124", {"start": v(-21.64, -53.88) * mm, "end": v(-2.69, -53.88) * mm});
            skLineSegment(sketch, "E125", {"start": v(-2.69, -53.88) * mm, "end": v(-2.69, -13.28) * mm});
            skLineSegment(sketch, "E126", {"start": v(-2.69, -13.28) * mm, "end": v(-21.64, -53.88) * mm});
            skLineSegment(sketch, "E127.MirrorCS", {"start": v(26.53, -53.46) * mm, "end": v(11.1, -12.4) * mm});
            skLineSegment(sketch, "E128.MirrorCS", {"start": v(22.26, -53.46) * mm, "end": v(2.78, -53.46) * mm});
            skLineSegment(sketch, "E129.MirrorCS", {"start": v(2.78, -53.46) * mm, "end": v(3.48, -13.07) * mm});
            skLineSegment(sketch, "E130.MirrorCS", {"start": v(3.48, -13.07) * mm, "end": v(22.26, -53.46) * mm});
            skLineSegment(sketch, "E131.MirrorCS", {"start": v(27.25, -12.4) * mm, "end": v(26.53, -53.46) * mm});
            skLineSegment(sketch, "E132.MirrorCS", {"start": v(27.25, -12.4) * mm, "end": v(11.1, -12.4) * mm});
            skLineSegment(sketch, "E133.MirrorCS", {"start": v(22.26, -64.39) * mm, "end": v(2.78, -64.39) * mm});
            skLineSegment(sketch, "E134.MirrorCS", {"start": v(-2.69, -113.1) * mm, "end": v(-22.17, -64.39) * mm});
            skLineSegment(sketch, "E135.MirrorCS", {"start": v(2.78, -64.39) * mm, "end": v(2.78, -113.1) * mm});
            skLineSegment(sketch, "E136.MirrorCS", {"start": v(2.78, -113.1) * mm, "end": v(22.26, -64.39) * mm});
            skLineSegment(sketch, "E137.MirrorCS", {"start": v(-2.69, -64.39) * mm, "end": v(-2.69, -113.1) * mm});
            skLineSegment(sketch, "E138.MirrorCS", {"start": v(26.53, -64.39) * mm, "end": v(8.48, -113.1) * mm});
            skLineSegment(sketch, "E139.MirrorCS", {"start": v(-26.45, -64.39) * mm, "end": v(-8.4, -113.1) * mm});
            skLineSegment(sketch, "E140.MirrorCS", {"start": v(-26.45, -113.1) * mm, "end": v(-26.45, -64.39) * mm});
            skLineSegment(sketch, "E141.MirrorCS", {"start": v(-26.45, -113.1) * mm, "end": v(-8.4, -113.1) * mm});
            skLineSegment(sketch, "E142.MirrorCS", {"start": v(26.53, -113.1) * mm, "end": v(8.48, -113.1) * mm});
            skLineSegment(sketch, "E143.MirrorCS", {"start": v(-22.17, -64.39) * mm, "end": v(-2.69, -64.39) * mm});
            skLineSegment(sketch, "E144.MirrorCS", {"start": v(26.53, -113.1) * mm, "end": v(26.53, -64.39) * mm});
            skLineSegment(sketch, "E145.MirrorCS", {"start": v(26.53, -121.17) * mm, "end": v(26.53, -169.87) * mm});
            skLineSegment(sketch, "E146.MirrorCS", {"start": v(26.53, -169.87) * mm, "end": v(8.48, -121.17) * mm});
            skLineSegment(sketch, "E147.MirrorCS", {"start": v(26.53, -121.17) * mm, "end": v(8.48, -121.17) * mm});
            skLineSegment(sketch, "E148.MirrorCS", {"start": v(2.78, -121.17) * mm, "end": v(22.26, -169.87) * mm});
            skLineSegment(sketch, "E149.MirrorCS", {"start": v(-2.69, -121.17) * mm, "end": v(-22.17, -169.87) * mm});
            skLineSegment(sketch, "E150.MirrorCS", {"start": v(-26.45, -121.17) * mm, "end": v(-26.45, -169.87) * mm});
            skLineSegment(sketch, "E151.MirrorCS", {"start": v(-2.69, -169.87) * mm, "end": v(-2.69, -121.17) * mm});
            skLineSegment(sketch, "E152.MirrorCS", {"start": v(-26.45, -169.87) * mm, "end": v(-8.4, -121.17) * mm});
            skLineSegment(sketch, "E153.MirrorCS", {"start": v(-22.17, -169.87) * mm, "end": v(-2.69, -169.87) * mm});
            skLineSegment(sketch, "E154.MirrorCS", {"start": v(-26.45, -121.17) * mm, "end": v(-8.4, -121.17) * mm});
            skLineSegment(sketch, "E155.MirrorCS", {"start": v(22.26, -169.87) * mm, "end": v(2.78, -169.87) * mm});
            skLineSegment(sketch, "E156.MirrorCS", {"start": v(2.78, -169.87) * mm, "end": v(2.78, -121.17) * mm});
            skSolve(sketch);
        }
        {
            var Q0;
            Q0=makeQuery(id+"F14.imprint","IMPRINT",FACE,{"disambiguationData":[TD([[makeQuery(id+"F14.imprint","IMPRINT",EDGE,{"derivedFrom":sQuery(id+"F14.wireOp",EDGE,"E121")}),-1.0]])]});
            var Q1;
            Q1=makeQuery(id+"F14.imprint","IMPRINT",FACE,{"disambiguationData":[TD([[makeQuery(id+"F14.imprint","IMPRINT",EDGE,{"derivedFrom":sQuery(id+"F14.wireOp",EDGE,"E124")}),1.0]])]});
            var Q2;
            Q2=makeQuery(id+"F14.imprint","IMPRINT",FACE,{"disambiguationData":[TD([[makeQuery(id+"F14.imprint","IMPRINT",EDGE,{"derivedFrom":sQuery(id+"F14.wireOp",EDGE,"E128.MirrorCS")}),-1.0]])]});
            var Q3;
            Q3=makeQuery(id+"F14.imprint","IMPRINT",FACE,{"disambiguationData":[TD([[makeQuery(id+"F14.imprint","IMPRINT",EDGE,{"derivedFrom":sQuery(id+"F14.wireOp",EDGE,"E127.MirrorCS")}),-1.0]])]});
            var Q4;
            Q4=makeQuery(id+"F14.imprint","IMPRINT",FACE,{"disambiguationData":[TD([[makeQuery(id+"F14.imprint","IMPRINT",EDGE,{"derivedFrom":sQuery(id+"F14.wireOp",EDGE,"E139.MirrorCS")}),-1.0]])]});
            var Q5;
            Q5=makeQuery(id+"F14.imprint","IMPRINT",FACE,{"disambiguationData":[TD([[makeQuery(id+"F14.imprint","IMPRINT",EDGE,{"derivedFrom":sQuery(id+"F14.wireOp",EDGE,"E134.MirrorCS")}),-1.0]])]});
            var Q6;
            Q6=makeQuery(id+"F14.imprint","IMPRINT",FACE,{"disambiguationData":[TD([[makeQuery(id+"F14.imprint","IMPRINT",EDGE,{"derivedFrom":sQuery(id+"F14.wireOp",EDGE,"E133.MirrorCS")}),1.0]])]});
            var Q7;
            Q7=makeQuery(id+"F14.imprint","IMPRINT",FACE,{"disambiguationData":[TD([[makeQuery(id+"F14.imprint","IMPRINT",EDGE,{"derivedFrom":sQuery(id+"F14.wireOp",EDGE,"E138.MirrorCS")}),1.0]])]});
            var Q8;
            Q8=makeQuery(id+"F14.imprint","IMPRINT",FACE,{"disambiguationData":[TD([[makeQuery(id+"F14.imprint","IMPRINT",EDGE,{"derivedFrom":sQuery(id+"F14.wireOp",EDGE,"E145.MirrorCS")}),-1.0]])]});
            var Q9;
            Q9=makeQuery(id+"F14.imprint","IMPRINT",FACE,{"disambiguationData":[TD([[makeQuery(id+"F14.imprint","IMPRINT",EDGE,{"derivedFrom":sQuery(id+"F14.wireOp",EDGE,"E148.MirrorCS")}),-1.0]])]});
            var Q10;
            Q10=makeQuery(id+"F14.imprint","IMPRINT",FACE,{"disambiguationData":[TD([[makeQuery(id+"F14.imprint","IMPRINT",EDGE,{"derivedFrom":sQuery(id+"F14.wireOp",EDGE,"E149.MirrorCS")}),1.0]])]});
            var Q11;
            Q11=makeQuery(id+"F14.imprint","IMPRINT",FACE,{"disambiguationData":[TD([[makeQuery(id+"F14.imprint","IMPRINT",EDGE,{"derivedFrom":sQuery(id+"F14.wireOp",EDGE,"E150.MirrorCS")}),1.0]])]});
            extrude(context, id + "F15", {"entities" : qUnion([Q0, Q1, Q2, Q3, Q4, Q5, Q6, Q7, Q8, Q9, Q10, Q11]), "oppositeDirection" : true, "depth" : 5 * mm, "offsetDistance" : 25 * mm});
        }
        {
            var Q0;
            Q0=makeQuery(id+"F15.opExtrude","SWEPT_BODY",BODY,{"disambiguationData":[OSD([sQuery(id+"F14.wireOp",EDGE,"E127.MirrorCS"),sQuery(id+"F14.wireOp",EDGE,"E131.MirrorCS"),sQuery(id+"F14.wireOp",EDGE,"E132.MirrorCS")])]});
            var Q1;
            Q1=makeQuery(id+"F15.opExtrude","SWEPT_BODY",BODY,{"disambiguationData":[OSD([sQuery(id+"F14.wireOp",EDGE,"E121"),sQuery(id+"F14.wireOp",EDGE,"E122"),sQuery(id+"F14.wireOp",EDGE,"E123")])]});
            var Q2;
            Q2=makeQuery(id+"F15.opExtrude","SWEPT_BODY",BODY,{"disambiguationData":[OSD([sQuery(id+"F14.wireOp",EDGE,"E124"),sQuery(id+"F14.wireOp",EDGE,"E125"),sQuery(id+"F14.wireOp",EDGE,"E126")])]});
            var Q3;
            Q3=makeQuery(id+"F15.opExtrude","SWEPT_BODY",BODY,{"disambiguationData":[OSD([sQuery(id+"F14.wireOp",EDGE,"E128.MirrorCS"),sQuery(id+"F14.wireOp",EDGE,"E129.MirrorCS"),sQuery(id+"F14.wireOp",EDGE,"E130.MirrorCS")])]});
            var Q4;
            Q4=makeQuery(id+"F15.opExtrude","SWEPT_BODY",BODY,{"disambiguationData":[OSD([sQuery(id+"F14.wireOp",EDGE,"E139.MirrorCS"),sQuery(id+"F14.wireOp",EDGE,"E140.MirrorCS"),sQuery(id+"F14.wireOp",EDGE,"E141.MirrorCS")])]});
            var Q5;
            Q5=makeQuery(id+"F15.opExtrude","SWEPT_BODY",BODY,{"disambiguationData":[OSD([sQuery(id+"F14.wireOp",EDGE,"E134.MirrorCS"),sQuery(id+"F14.wireOp",EDGE,"E137.MirrorCS"),sQuery(id+"F14.wireOp",EDGE,"E143.MirrorCS")])]});
            var Q6;
            Q6=makeQuery(id+"F15.opExtrude","SWEPT_BODY",BODY,{"disambiguationData":[OSD([sQuery(id+"F14.wireOp",EDGE,"E133.MirrorCS"),sQuery(id+"F14.wireOp",EDGE,"E135.MirrorCS"),sQuery(id+"F14.wireOp",EDGE,"E136.MirrorCS")])]});
            var Q7;
            Q7=makeQuery(id+"F15.opExtrude","SWEPT_BODY",BODY,{"disambiguationData":[OSD([sQuery(id+"F14.wireOp",EDGE,"E138.MirrorCS"),sQuery(id+"F14.wireOp",EDGE,"E142.MirrorCS"),sQuery(id+"F14.wireOp",EDGE,"E144.MirrorCS")])]});
            var Q8;
            Q8=makeQuery(id+"F15.opExtrude","SWEPT_BODY",BODY,{"disambiguationData":[OSD([sQuery(id+"F14.wireOp",EDGE,"E150.MirrorCS"),sQuery(id+"F14.wireOp",EDGE,"E152.MirrorCS"),sQuery(id+"F14.wireOp",EDGE,"E154.MirrorCS")])]});
            var Q9;
            Q9=makeQuery(id+"F15.opExtrude","SWEPT_BODY",BODY,{"disambiguationData":[OSD([sQuery(id+"F14.wireOp",EDGE,"E149.MirrorCS"),sQuery(id+"F14.wireOp",EDGE,"E151.MirrorCS"),sQuery(id+"F14.wireOp",EDGE,"E153.MirrorCS")])]});
            var Q10;
            Q10=makeQuery(id+"F15.opExtrude","SWEPT_BODY",BODY,{"disambiguationData":[OSD([sQuery(id+"F14.wireOp",EDGE,"E148.MirrorCS"),sQuery(id+"F14.wireOp",EDGE,"E155.MirrorCS"),sQuery(id+"F14.wireOp",EDGE,"E156.MirrorCS")])]});
            var Q11;
            Q11=makeQuery(id+"F15.opExtrude","SWEPT_BODY",BODY,{"disambiguationData":[OSD([sQuery(id+"F14.wireOp",EDGE,"E145.MirrorCS"),sQuery(id+"F14.wireOp",EDGE,"E146.MirrorCS"),sQuery(id+"F14.wireOp",EDGE,"E147.MirrorCS")])]});
            var Q12;
            Q12=makeQuery(id+"F1.opExtrude","SWEPT_BODY",BODY,{"disambiguationData":[OSD([sQuery(id+"F0.wireOp",EDGE,"E0.bottom"),sQuery(id+"F0.wireOp",EDGE,"E0.top"),sQuery(id+"F0.wireOp",EDGE,"E0.left"),sQuery(id+"F0.wireOp",EDGE,"E0.right"),sQuery(id+"F0.wireOp",EDGE,"E1.bottom"),sQuery(id+"F0.wireOp",EDGE,"E1.top"),sQuery(id+"F0.wireOp",EDGE,"E1.left"),sQuery(id+"F0.wireOp",EDGE,"E1.right")])]});
            booleanBodies(context, id + "F16", {"operationType" : BooleanOperationType.SUBTRACTION, "tools" : qUnion([Q0, Q1, Q2, Q3, Q4, Q5, Q6, Q7, Q8, Q9, Q10, Q11]), "targets" : qUnion([Q12])});
        }
        {
            var Q0;
            Q0=makeQuery(id+"F0.imprint","IMPRINT",FACE,{"disambiguationData":[TD([[makeQuery(id+"F0.imprint","IMPRINT",EDGE,{"derivedFrom":sQuery(id+"F0.wireOp",EDGE,"E0.bottom")}),1.0]])]});
            var sketch = newSketch(context, id + "F17", { "sketchPlane" : qUnion([Q0])});
            skLineSegment(sketch, "E157.bottom", {"start": v(-31.73, 25.65) * mm, "end": v(31.73, 25.65) * mm});
            skLineSegment(sketch, "E157.top", {"start": v(-31.73, -25.65) * mm, "end": v(31.73, -25.65) * mm});
            skLineSegment(sketch, "E157.left", {"start": v(-31.73, 25.65) * mm, "end": v(-31.73, -25.65) * mm});
            skLineSegment(sketch, "E157.right", {"start": v(31.73, 25.65) * mm, "end": v(31.73, -25.65) * mm});
            skSolve(sketch);
        }
        {
            var Q0;
            Q0 = qSketchRegion(id + "F17", true);
            extrude(context, id + "F18", {"entities" : qUnion([Q0]), "depth" : 8 * mm, "offsetDistance" : 25 * mm});
        }
        {
            var Q0;
            Q0=makeQuery(id+"F18.opExtrude","CAP_FACE",FACE,{"disambiguationData":[OSD([sQuery(id+"F17.wireOp",EDGE,"E157.bottom"),sQuery(id+"F17.wireOp",EDGE,"E157.top"),sQuery(id+"F17.wireOp",EDGE,"E157.left"),sQuery(id+"F17.wireOp",EDGE,"E157.right")])],"isStart":false});
            var sketch = newSketch(context, id + "F19", { "sketchPlane" : qUnion([Q0])});
            skLineSegment(sketch, "E158.bottom", {"start": v(-30.5, 23.5) * mm, "end": v(30.5, 23.5) * mm});
            skLineSegment(sketch, "E158.top", {"start": v(-30.5, -23.5) * mm, "end": v(30.5, -23.5) * mm});
            skLineSegment(sketch, "E158.left", {"start": v(-30.5, 23.5) * mm, "end": v(-30.5, -23.5) * mm});
            skLineSegment(sketch, "E158.right", {"start": v(30.5, 23.5) * mm, "end": v(30.5, -23.5) * mm});
            skSolve(sketch);
        }
        {
            var Q0;
            Q0 = qSketchRegion(id + "F19", true);
            extrude(context, id + "F20", {"entities" : qUnion([Q0]), "oppositeDirection" : true, "depth" : 20 * mm, "offsetDistance" : 25 * mm});
        }
        {
            var Q0;
            Q0=makeQuery(id+"F20.opExtrude","SWEPT_BODY",BODY,{"disambiguationData":[OSD([sQuery(id+"F19.wireOp",EDGE,"E158.bottom"),sQuery(id+"F19.wireOp",EDGE,"E158.top"),sQuery(id+"F19.wireOp",EDGE,"E158.left"),sQuery(id+"F19.wireOp",EDGE,"E158.right")])]});
            var Q1;
            Q1=makeQuery(id+"F18.opExtrude","SWEPT_BODY",BODY,{"disambiguationData":[OSD([sQuery(id+"F17.wireOp",EDGE,"E157.bottom"),sQuery(id+"F17.wireOp",EDGE,"E157.top"),sQuery(id+"F17.wireOp",EDGE,"E157.left"),sQuery(id+"F17.wireOp",EDGE,"E157.right")])]});
            booleanBodies(context, id + "F21", {"operationType" : BooleanOperationType.SUBTRACTION, "tools" : qUnion([Q0]), "targets" : qUnion([Q1])});
        }
    });
